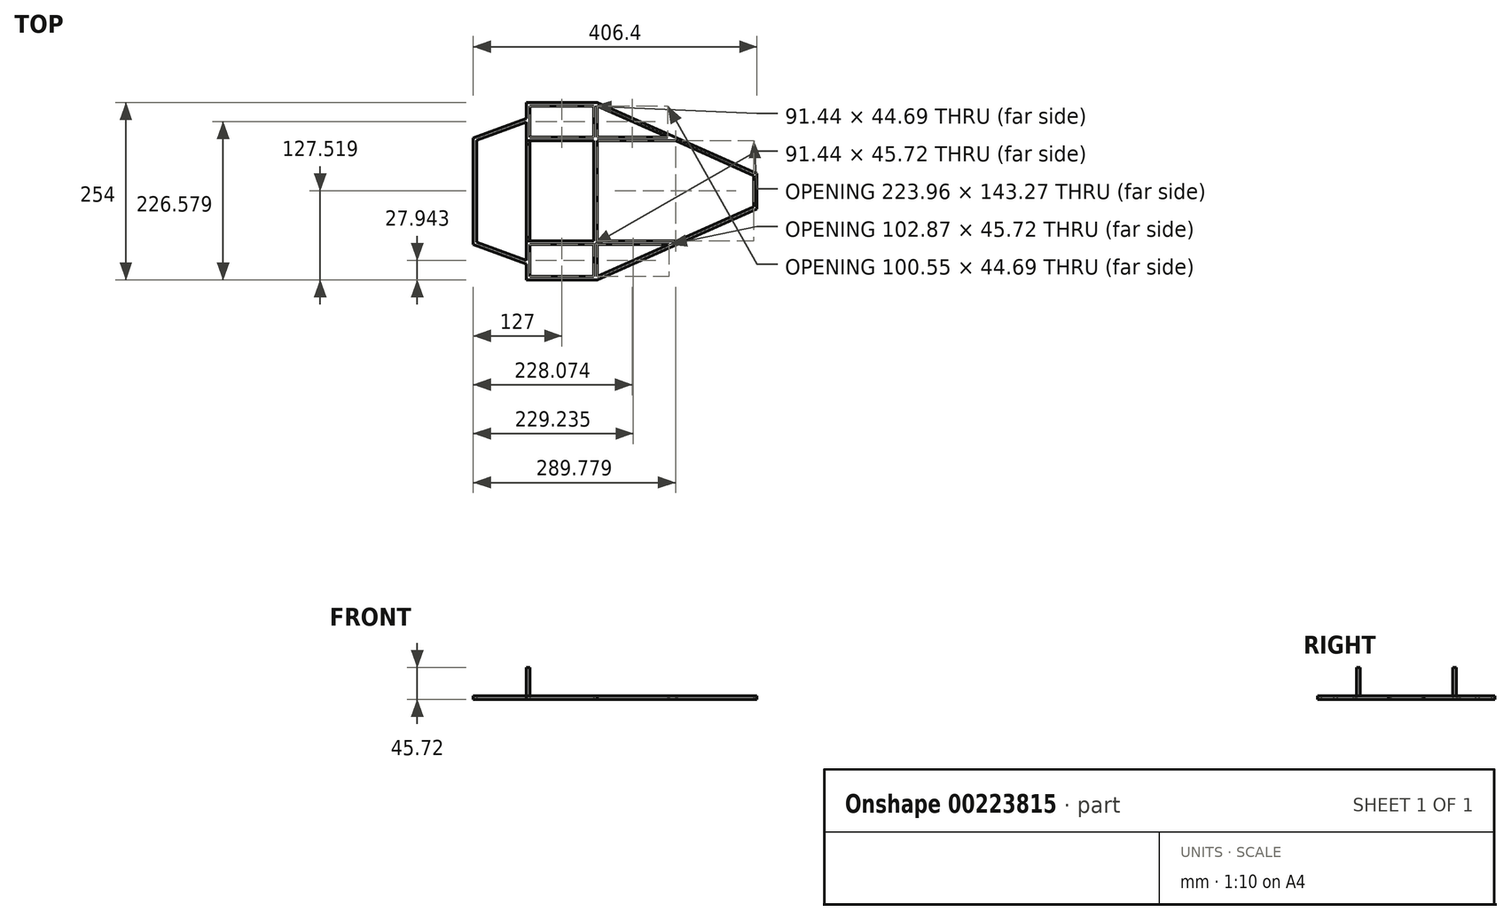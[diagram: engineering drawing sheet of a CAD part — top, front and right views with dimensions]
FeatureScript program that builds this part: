
annotation { "Feature Type Name" : "Feature", "Feature Type Description" : "" }
export const myFeature = defineFeature(function(context is Context, id is Id, definition is map)
    precondition{}
    {
        {
            var Q0;
            Q0=qCreatedBy(makeId("Top.planeOp"),FACE);
            var sketch = newSketch(context, id + "F0", { "sketchPlane" : qUnion([Q0])});
            skLineSegment(sketch, "E0.bottom", {"start": v(-96.52, 131.83) * mm, "end": v(5.08, 131.83) * mm});
            skLineSegment(sketch, "E0.top", {"start": v(-96.52, -122.17) * mm, "end": v(5.08, -122.17) * mm});
            skLineSegment(sketch, "E0.left", {"start": v(-96.52, 131.83) * mm, "end": v(-96.52, -122.17) * mm});
            skLineSegment(sketch, "E0.right", {"start": v(5.08, 131.83) * mm, "end": v(5.08, -122.17) * mm});
            skLineSegment(sketch, "E1", {"start": v(-91.44, 131.83) * mm, "end": v(-91.44, -122.17) * mm});
            skLineSegment(sketch, "E2", {"start": v(0, 131.83) * mm, "end": v(0, -122.17) * mm});
            skLineSegment(sketch, "E3", {"start": v(-91.44, 126.75) * mm, "end": v(0, 126.75) * mm});
            skLineSegment(sketch, "E4", {"start": v(-91.44, -117.09) * mm, "end": v(0, -117.09) * mm});
            skLineSegment(sketch, "E5", {"start": v(-91.44, -66.29) * mm, "end": v(0, -66.29) * mm});
            skLineSegment(sketch, "E6", {"start": v(-91.44, -71.37) * mm, "end": v(0, -71.37) * mm});
            skLineSegment(sketch, "E7", {"start": v(-91.44, 76.98) * mm, "end": v(0, 76.98) * mm});
            skLineSegment(sketch, "E8", {"start": v(-91.44, 82.06) * mm, "end": v(0, 82.06) * mm});
            skLineSegment(sketch, "E9", {"start": v(5.08, -122.17) * mm, "end": v(233.68, -20.57) * mm});
            skLineSegment(sketch, "E10", {"start": v(5.08, -117.09) * mm, "end": v(229.04, -17.55) * mm});
            skLineSegment(sketch, "E11", {"start": v(229.04, -17.55) * mm, "end": v(233.68, -20.57) * mm});
            skLineSegment(sketch, "E12", {"start": v(233.68, -20.57) * mm, "end": v(233.68, 30.23) * mm});
            skLineSegment(sketch, "E13", {"start": v(5.08, 131.83) * mm, "end": v(233.68, 30.23) * mm});
            skLineSegment(sketch, "E14.MirrorCS", {"start": v(5.08, 126.75) * mm, "end": v(229.04, 27.22) * mm});
            skLineSegment(sketch, "E15", {"start": v(229.04, 27.22) * mm, "end": v(229.04, -17.55) * mm});
            skLineSegment(sketch, "E16", {"start": v(229.04, 27.22) * mm, "end": v(233.68, 30.23) * mm});
            skLineSegment(sketch, "E17", {"start": v(-172.72, 81.03) * mm, "end": v(-172.72, -71.37) * mm});
            skLineSegment(sketch, "E18", {"start": v(-172.72, 81.03) * mm, "end": v(-96.52, 108.97) * mm});
            skLineSegment(sketch, "E19", {"start": v(-172.72, -71.37) * mm, "end": v(-96.52, -99.3) * mm});
            skLineSegment(sketch, "E20", {"start": v(-96.52, 103.9) * mm, "end": v(-167.64, 77.82) * mm});
            skLineSegment(sketch, "E21", {"start": v(-96.52, -94.23) * mm, "end": v(-167.64, -68.15) * mm});
            skLineSegment(sketch, "E22", {"start": v(-167.64, -68.15) * mm, "end": v(-167.64, 77.82) * mm});
            skLineSegment(sketch, "E23", {"start": v(-167.64, 77.82) * mm, "end": v(-172.72, 81.03) * mm});
            skLineSegment(sketch, "E24", {"start": v(-172.72, -71.37) * mm, "end": v(-167.64, -68.15) * mm});
            skLineSegment(sketch, "E25", {"start": v(5.08, 82.06) * mm, "end": v(105.63, 82.06) * mm});
            skLineSegment(sketch, "E26", {"start": v(5.08, 76.98) * mm, "end": v(117.06, 76.98) * mm});
            skLineSegment(sketch, "E27", {"start": v(5.08, -66.29) * mm, "end": v(119.38, -66.29) * mm});
            skLineSegment(sketch, "E28", {"start": v(5.08, -71.37) * mm, "end": v(107.95, -71.37) * mm});
            skPoint(sketch, "E29", {"position": v(-91.44, -66.29) * mm});
            skPoint(sketch, "E30", {"position": v(-91.44, -61.2) * mm});
            skPoint(sketch, "E31", {"position": v(-96.52, -61.2) * mm});
            skPoint(sketch, "E32", {"position": v(-96.52, -66.29) * mm});
            skPoint(sketch, "E33", {"position": v(-91.44, 76.98) * mm});
            skPoint(sketch, "E34", {"position": v(-96.52, 76.98) * mm});
            skPoint(sketch, "E35", {"position": v(-96.52, 71.9) * mm});
            skPoint(sketch, "E36", {"position": v(-91.44, 71.9) * mm});
            skSolve(sketch);
        }
        {
            var Q0;
            Q0=qCreatedBy(makeId("Top.planeOp"),FACE);
            var sketch = newSketch(context, id + "F1", { "sketchPlane" : qUnion([Q0])});
            skLineSegment(sketch, "E37.bottom", {"start": v(-91.44, 76.99) * mm, "end": v(-96.52, 76.99) * mm});
            skLineSegment(sketch, "E37.top", {"start": v(-91.44, 71.9) * mm, "end": v(-96.52, 71.9) * mm});
            skLineSegment(sketch, "E37.left", {"start": v(-91.44, 76.99) * mm, "end": v(-91.44, 71.9) * mm});
            skLineSegment(sketch, "E37.right", {"start": v(-96.52, 76.99) * mm, "end": v(-96.52, 71.9) * mm});
            skLineSegment(sketch, "E38.bottom", {"start": v(-91.44, -66.29) * mm, "end": v(-96.52, -66.29) * mm});
            skLineSegment(sketch, "E38.top", {"start": v(-91.44, -61.2) * mm, "end": v(-96.52, -61.2) * mm});
            skLineSegment(sketch, "E38.left", {"start": v(-91.44, -66.29) * mm, "end": v(-91.44, -61.2) * mm});
            skLineSegment(sketch, "E38.right", {"start": v(-96.52, -66.29) * mm, "end": v(-96.52, -61.2) * mm});
            skSolve(sketch);
        }
        {
            var Q0;
            Q0=makeQuery(id+"F1.imprint","IMPRINT",FACE,{"disambiguationData":[TD([[makeQuery(id+"F1.imprint","IMPRINT",EDGE,{"derivedFrom":sQuery(id+"F1.wireOp",EDGE,"E37.bottom")}),1.0]])]});
            extrude(context, id + "F2", {"entities" : qUnion([Q0]), "depth" : 45.72 * mm});
        }
        {
            var Q0;
            Q0 = qSketchRegion(id + "F0", true);
            var Q1;
            {var subQ0=sQuery(id+"F0.wireOp",EDGE,"E5");Q1=makeQuery(id+"F0.imprint","IMPRINT",FACE,{"disambiguationData":[TD([[makeQuery(id+"F0.imprint","IMPRINT",EDGE,{"derivedFrom":subQ0}),-1.0]])]});}
            var Q2;
            {var subQ0=sQuery(id+"F0.wireOp",EDGE,"E7");Q2=makeQuery(id+"F0.imprint","IMPRINT",FACE,{"disambiguationData":[TD([[makeQuery(id+"F0.imprint","IMPRINT",EDGE,{"derivedFrom":subQ0}),1.0]])]});}
            var Q3;
            {var subQ0=sQuery(id+"F0.wireOp",EDGE,"E25");Q3=makeQuery(id+"F0.imprint","IMPRINT",FACE,{"disambiguationData":[TD([[makeQuery(id+"F0.imprint","IMPRINT",EDGE,{"derivedFrom":subQ0}),-1.0]])]});}
            var Q4;
            {var subQ0=sQuery(id+"F0.wireOp",EDGE,"E27");Q4=makeQuery(id+"F0.imprint","IMPRINT",FACE,{"disambiguationData":[TD([[makeQuery(id+"F0.imprint","IMPRINT",EDGE,{"derivedFrom":subQ0}),-1.0]])]});}
            extrude(context, id + "F3", {"entities" : qUnion([Q0, Q1, Q2, Q3, Q4]), "depth" : 5.08 * mm});
        }
        {
            var Q0;
            Q0=makeQuery(id+"F1.imprint","IMPRINT",FACE,{"disambiguationData":[TD([[makeQuery(id+"F1.imprint","IMPRINT",EDGE,{"derivedFrom":sQuery(id+"F1.wireOp",EDGE,"E38.bottom")}),-1.0]])]});
            extrude(context, id + "F4", {"entities" : qUnion([Q0]), "operationType" : NewBodyOperationType.ADD, "depth" : 45.72 * mm});
        }
    });
